# Revit family: Sanitary_Basins_RAK-SERIES-600-SEMI-RECESSED
name_source: partatom
category: Plumbing Fixtures
units: mm (PartAtom-declared; Revit-internal decimal feet)

## family parameters
Cut with Voids When Loaded = No
Host = Face
OmniClass Number = 23.45.00.00
OmniClass Title = Sanitary, Laundry, and Cleaning Equipment
Part Type = Normal
Room Calculation Point = No
Round Connector Dimension = Use Diameter
Shared = No

## types (1)
- RAK SERIES 600 WASH BASIN SEMI RECESSED 42CM
    Default Elevation = 1219 mm
    Installation instructions = https://www.rakceramics.com
    MEP Diameter = 80  [stored 0.262467 ft]
    Manufacturer = RAK Ceramics
    Product certification = https://www.rakceramics.com
    Product data url = https://www.bimobject.com
    Product url = https://www.rakceramics.com
    Technical description = https://www.rakceramics.com
    Youtube clip = https://www.rakceramics.com

note: [stored X ft] marks values corroborated as IEEE doubles in the binary element streams (Revit-internal decimal feet)

## geometry (parser evidence)
native form markers: Sweep x4
no freeform markers — native parametric forms only
